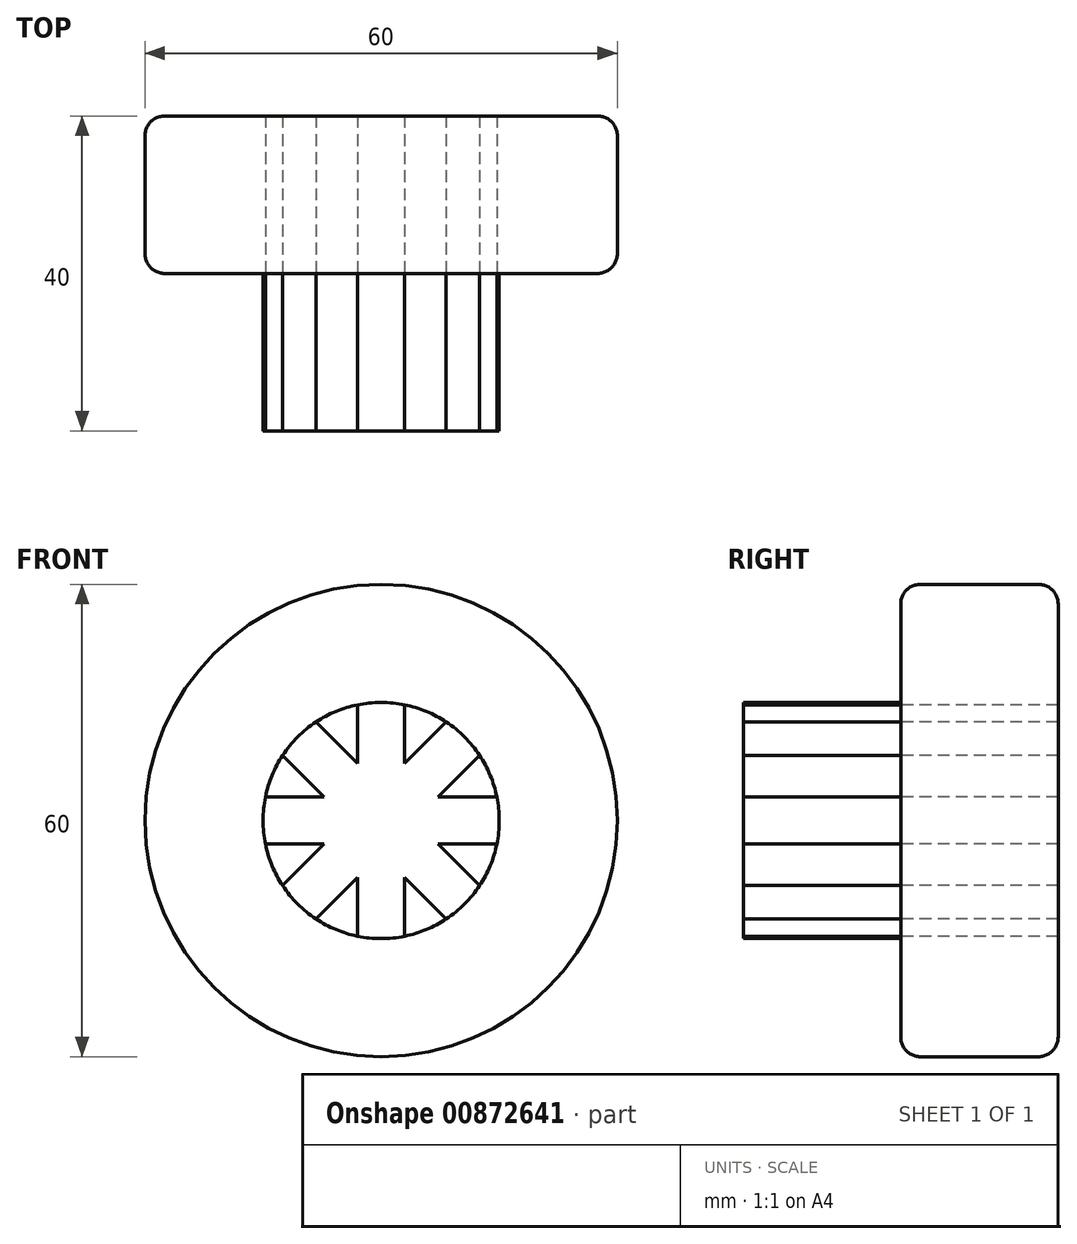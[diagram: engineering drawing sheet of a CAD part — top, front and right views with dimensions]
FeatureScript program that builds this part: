
annotation { "Feature Type Name" : "Feature", "Feature Type Description" : "" }
export const myFeature = defineFeature(function(context is Context, id is Id, definition is map)
    precondition{}
    {
        {
            var Q0;
            Q0=qCreatedBy(makeId("Front.planeOp"),FACE);
            var sketch = newSketch(context, id + "F0", { "sketchPlane" : qUnion([Q0])});
            skCircle(sketch, "E0", {"center": v(0, 0) * mm, "radius": 30 * mm});
            skCircle(sketch, "E1", {"center": v(0, 0) * mm, "radius": 15 * mm});
            skLineSegment(sketch, "E2.MirrorCS", {"start": v(-3, 7.24) * mm, "end": v(-3, 14.7) * mm});
            skLineSegment(sketch, "E3.1.0", {"start": v(-7.24, 3) * mm, "end": v(-12.51, 8.27) * mm});
            skLineSegment(sketch, "E3.1.1", {"start": v(-3, 7.24) * mm, "end": v(-8.27, 12.51) * mm});
            skLineSegment(sketch, "E3.2.0", {"start": v(-7.24, -3) * mm, "end": v(-14.7, -3) * mm});
            skLineSegment(sketch, "E3.2.1", {"start": v(-7.24, 3) * mm, "end": v(-14.7, 3) * mm});
            skLineSegment(sketch, "E3.3.1", {"start": v(-7.24, -3) * mm, "end": v(-12.51, -8.27) * mm});
            skPoint(sketch, "E4.orphan", {"position": v(2.12, -2.12) * mm});
            skPoint(sketch, "E5.orphan", {"position": v(2.12, 2.12) * mm});
            skPoint(sketch, "E6.orphan", {"position": v(3, 0) * mm});
            skPoint(sketch, "E7.orphan", {"position": v(0, -3) * mm});
            skPoint(sketch, "E8.orphan", {"position": v(-2.12, 2.12) * mm});
            skPoint(sketch, "E9.orphan", {"position": v(-2.12, -2.12) * mm});
            skPoint(sketch, "E10.orphan", {"position": v(0, 3) * mm});
            skPoint(sketch, "E11.orphan", {"position": v(-3, 0) * mm});
            skLineSegment(sketch, "E12.1.4.0", {"start": v(3, -7.24) * mm, "end": v(3, -14.7) * mm});
            skLineSegment(sketch, "E12.3.4.0", {"start": v(-3, -7.24) * mm, "end": v(-3, -14.7) * mm});
            skLineSegment(sketch, "E12.1.5.0", {"start": v(7.24, -3) * mm, "end": v(12.51, -8.27) * mm});
            skLineSegment(sketch, "E12.3.5.0", {"start": v(3, -7.24) * mm, "end": v(8.27, -12.51) * mm});
            skLineSegment(sketch, "E12.1.6.0", {"start": v(7.24, 3) * mm, "end": v(14.7, 3) * mm});
            skLineSegment(sketch, "E12.3.6.0", {"start": v(7.24, -3) * mm, "end": v(14.7, -3) * mm});
            skLineSegment(sketch, "E12.1.7.0", {"start": v(3, 7.24) * mm, "end": v(8.27, 12.51) * mm});
            skLineSegment(sketch, "E12.3.7.0", {"start": v(7.24, 3) * mm, "end": v(12.51, 8.27) * mm});
            skLineSegment(sketch, "E13.trimOffspring", {"start": v(3, 7.24) * mm, "end": v(3, 14.7) * mm});
            skLineSegment(sketch, "E14.trimOffspring", {"start": v(-3, -7.24) * mm, "end": v(-8.27, -12.51) * mm});
            skSolve(sketch);
        }
        {
            var Q0;
            {var subQ12=sQuery(id+"F0.wireOp",EDGE,"E2.MirrorCS");Q0=makeQuery(id+"F0.imprint","IMPRINT",FACE,{"disambiguationData":[TD([[makeQuery(id+"F0.imprint","IMPRINT",EDGE,{"derivedFrom":subQ12}),-1.0]])]});}
            extrude(context, id + "F1", {"entities" : qUnion([Q0]), "depth" : 20 * mm, "offsetDistance" : 25 * mm});
        }
        {
            var Q0;
            Q0 = qSketchRegion(id + "F0", true);
            var Q1;
            Q1=makeQuery(id+"F1.opExtrude","CAP_FACE",FACE,{"disambiguationData":[OSD([sQuery(id+"F0.wireOp",EDGE,"E1"),sQuery(id+"F0.wireOp",EDGE,"E2.MirrorCS"),sQuery(id+"F0.wireOp",EDGE,"E3.1.0"),sQuery(id+"F0.wireOp",EDGE,"E3.1.1"),sQuery(id+"F0.wireOp",EDGE,"E3.2.0"),sQuery(id+"F0.wireOp",EDGE,"E3.2.1"),sQuery(id+"F0.wireOp",EDGE,"E3.3.1"),sQuery(id+"F0.wireOp",EDGE,"E12.1.4.0"),sQuery(id+"F0.wireOp",EDGE,"E12.3.4.0"),sQuery(id+"F0.wireOp",EDGE,"E12.1.5.0"),sQuery(id+"F0.wireOp",EDGE,"E12.3.5.0"),sQuery(id+"F0.wireOp",EDGE,"E12.1.6.0"),sQuery(id+"F0.wireOp",EDGE,"E12.3.6.0"),sQuery(id+"F0.wireOp",EDGE,"E12.1.7.0"),sQuery(id+"F0.wireOp",EDGE,"E12.3.7.0"),sQuery(id+"F0.wireOp",EDGE,"E13.trimOffspring"),sQuery(id+"F0.wireOp",EDGE,"E14.trimOffspring")])],"isStart":true});
            extrude(context, id + "F2", {"entities" : qUnion([Q0, Q1]), "operationType" : NewBodyOperationType.ADD, "oppositeDirection" : true, "depth" : 20 * mm, "offsetDistance" : 25 * mm});
        }
        {
            var Q0;
            Q0=makeQuery(id+"F2.opExtrude","CAP_EDGE",EDGE,{"disambiguationData":[OSD([sQuery(id+"F0.wireOp",EDGE,"E0")])],"isStart":true});
            var Q1;
            Q1=makeQuery(id+"F2.opExtrude","CAP_EDGE",EDGE,{"disambiguationData":[OSD([sQuery(id+"F0.wireOp",EDGE,"E0")])],"isStart":false});
            fillet(context, id + "F3", {"entities" : qUnion([Q0, Q1]), "radius" : 2.5 * mm, "tangentPropagation" : true, "allowEdgeOverflow" : false});
        }
    });
